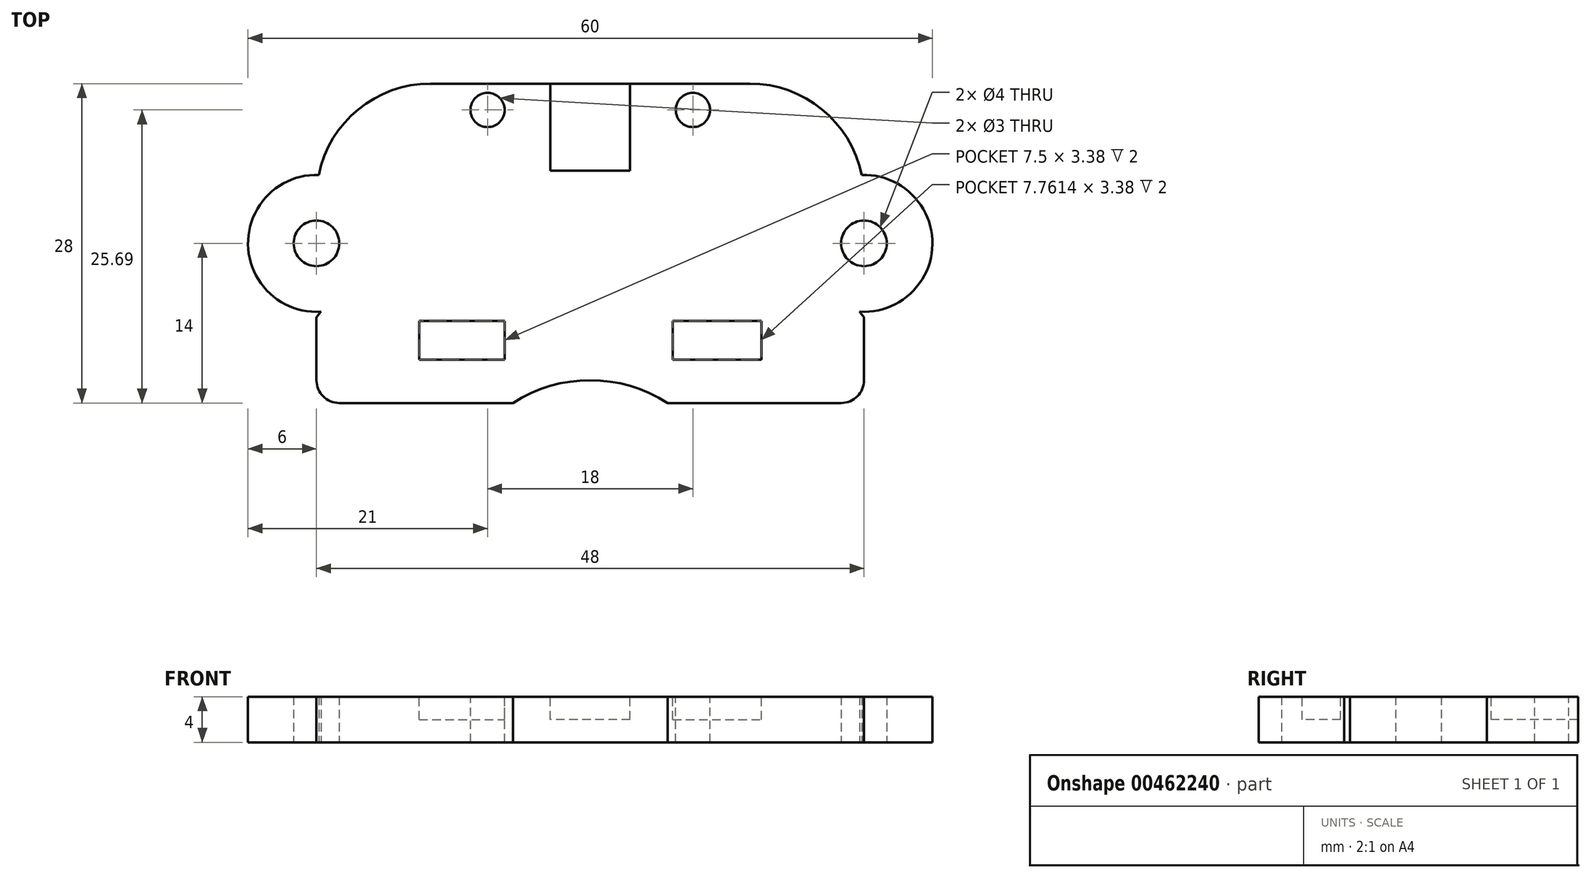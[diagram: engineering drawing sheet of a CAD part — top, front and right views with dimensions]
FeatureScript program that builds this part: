
annotation { "Feature Type Name" : "Feature", "Feature Type Description" : "" }
export const myFeature = defineFeature(function(context is Context, id is Id, definition is map)
    precondition{}
    {
        {
            var Q0;
            Q0=qCreatedBy(makeId("Top.planeOp"),FACE);
            var sketch = newSketch(context, id + "F0", { "sketchPlane" : qUnion([Q0])});
            skLineSegment(sketch, "E0.bottom", {"start": v(22, -14) * mm, "end": v(-22, -14) * mm});
            skLineSegment(sketch, "E0.top", {"start": v(14, 14) * mm, "end": v(-14, 14) * mm});
            skLineSegment(sketch, "E0.left", {"start": v(24, -12) * mm, "end": v(24, 4) * mm});
            skLineSegment(sketch, "E0.right", {"start": v(-24, -12) * mm, "end": v(-24, 4) * mm});
            skPoint(sketch, "E0.middle", {"position": v(0, 0) * mm});
            skPoint(sketch, "E1", {"position": v(-24, 0) * mm});
            skPoint(sketch, "E2", {"position": v(24, 0) * mm});
            skPoint(sketch, "E3", {"position": v(76.27, -6.83) * mm});
            skCircle(sketch, "E4", {"center": v(0, -24.5) * mm, "radius": 30 * mm});
            skCircle(sketch, "E5", {"center": v(0, -24.5) * mm, "radius": 12.5 * mm});
            skCircle(sketch, "E6", {"center": v(-24, 0) * mm, "radius": 4 * mm});
            skCircle(sketch, "E7", {"center": v(24, 0) * mm, "radius": 4 * mm});
            skCircle(sketch, "E8.0", {"center": v(-24, 0) * mm, "radius": 6 * mm});
            skCircle(sketch, "E9.0", {"center": v(24, 0) * mm, "radius": 6 * mm});
            skPoint(sketch, "E10.visualSharp", {"position": v(-24, 14) * mm});
            skArc(sketch, "E10.filletArc", {"start": v(-14, 14) * mm, "mid": v(-21.07, 11.07) * mm, "end": v(-24, 4) * mm});
            skPoint(sketch, "E11.visualSharp", {"position": v(24, 14) * mm});
            skArc(sketch, "E11.filletArc", {"start": v(24, 4) * mm, "mid": v(21.07, 11.07) * mm, "end": v(14, 14) * mm});
            skPoint(sketch, "E12.visualSharp", {"position": v(-24, -14) * mm});
            skArc(sketch, "E12.filletArc", {"start": v(-24, -12) * mm, "mid": v(-23.41, -13.41) * mm, "end": v(-22, -14) * mm});
            skPoint(sketch, "E13.visualSharp", {"position": v(24, -14) * mm});
            skArc(sketch, "E13.filletArc", {"start": v(22, -14) * mm, "mid": v(23.41, -13.41) * mm, "end": v(24, -12) * mm});
            skSolve(sketch);
        }
        {
            var Q0;
            {var subQ16=sQuery(id+"F0.wireOp",EDGE,"E12.filletArc");Q0=makeQuery(id+"F0.imprint","IMPRINT",FACE,{"disambiguationData":[TD([[makeQuery(id+"F0.imprint","IMPRINT",EDGE,{"derivedFrom":subQ16}),1.0]])]});}
            var Q1;
            {var subQ7=sQuery(id+"F0.wireOp",EDGE,"E0.top");Q1=makeQuery(id+"F0.imprint","IMPRINT",FACE,{"disambiguationData":[TD([[makeQuery(id+"F0.imprint","IMPRINT",EDGE,{"derivedFrom":subQ7}),1.0]])]});}
            var Q2;
            {var subQ0=sQuery(id+"F0.wireOp",EDGE,"E7");var subQ1=sQuery(id+"F0.wireOp",EDGE,"E0.left");var subQ3=makeQuery(id+"F0.imprint","INTERSECT",VERTEX,{"derivedFrom":[subQ1,subQ0]});Q2=makeQuery(id+"F0.imprint","IMPRINT",FACE,{"disambiguationData":[TD([[makeQuery(id+"F0.imprint","IMPRINT",EDGE,{"disambiguationData":[TD([[subQ3,-1.0]])],"derivedFrom":subQ1}),-1.0]])]});}
            var Q3;
            {var subQ0=sQuery(id+"F0.wireOp",EDGE,"E8.0");var subQ1=sQuery(id+"F0.wireOp",EDGE,"E4");var subQ2=makeQuery(id+"F0.imprint","INTERSECT",VERTEX,{"disambiguationData":[OD(0.0)],"derivedFrom":[subQ1,subQ0]});Q3=makeQuery(id+"F0.imprint","IMPRINT",FACE,{"disambiguationData":[TD([[makeQuery(id+"F0.imprint","IMPRINT",EDGE,{"disambiguationData":[TD([[subQ2,-1.0]])],"derivedFrom":subQ1}),1.0]])]});}
            var Q4;
            {var subQ2=sQuery(id+"F0.wireOp",EDGE,"E0.left");var subQ5=sQuery(id+"F0.wireOp",EDGE,"E9.0");var subQ9=makeQuery(id+"F0.imprint","INTERSECT",VERTEX,{"derivedFrom":[subQ2,subQ5]});Q4=makeQuery(id+"F0.imprint","IMPRINT",FACE,{"disambiguationData":[TD([[makeQuery(id+"F0.imprint","IMPRINT",EDGE,{"disambiguationData":[TD([[subQ9,-1.0]])],"derivedFrom":subQ2}),1.0]])]});}
            var Q5;
            {var subQ0=sQuery(id+"F0.wireOp",EDGE,"E8.0");var subQ1=sQuery(id+"F0.wireOp",EDGE,"E0.right");var subQ2=makeQuery(id+"F0.imprint","INTERSECT",VERTEX,{"derivedFrom":[subQ1,subQ0]});Q5=makeQuery(id+"F0.imprint","IMPRINT",FACE,{"disambiguationData":[TD([[makeQuery(id+"F0.imprint","IMPRINT",EDGE,{"disambiguationData":[TD([[subQ2,-1.0]])],"derivedFrom":subQ1}),1.0]])]});}
            var Q6;
            {var subQ0=sQuery(id+"F0.wireOp",EDGE,"E9.0");var subQ1=sQuery(id+"F0.wireOp",EDGE,"E0.left");var subQ2=makeQuery(id+"F0.imprint","INTERSECT",VERTEX,{"derivedFrom":[subQ1,subQ0]});Q6=makeQuery(id+"F0.imprint","IMPRINT",FACE,{"disambiguationData":[TD([[makeQuery(id+"F0.imprint","IMPRINT",EDGE,{"disambiguationData":[TD([[subQ2,-1.0]])],"derivedFrom":subQ1}),-1.0]])]});}
            var Q7;
            {var subQ2=sQuery(id+"F0.wireOp",EDGE,"E0.right");var subQ5=sQuery(id+"F0.wireOp",EDGE,"E8.0");var subQ6=makeQuery(id+"F0.imprint","INTERSECT",VERTEX,{"derivedFrom":[subQ2,subQ5]});Q7=makeQuery(id+"F0.imprint","IMPRINT",FACE,{"disambiguationData":[TD([[makeQuery(id+"F0.imprint","IMPRINT",EDGE,{"disambiguationData":[TD([[subQ6,-1.0]])],"derivedFrom":subQ2}),-1.0]])]});}
            var Q8;
            {var subQ0=sQuery(id+"F0.wireOp",EDGE,"E7");var subQ1=sQuery(id+"F0.wireOp",EDGE,"E0.left");var subQ3=makeQuery(id+"F0.imprint","INTERSECT",VERTEX,{"derivedFrom":[subQ1,subQ0]});Q8=makeQuery(id+"F0.imprint","IMPRINT",FACE,{"disambiguationData":[TD([[makeQuery(id+"F0.imprint","IMPRINT",EDGE,{"disambiguationData":[TD([[subQ3,-1.0]])],"derivedFrom":subQ1}),1.0]])]});}
            var Q9;
            {var subQ0=sQuery(id+"F0.wireOp",EDGE,"E6");var subQ1=sQuery(id+"F0.wireOp",EDGE,"E0.right");var subQ3=makeQuery(id+"F0.imprint","INTERSECT",VERTEX,{"derivedFrom":[subQ1,subQ0]});Q9=makeQuery(id+"F0.imprint","IMPRINT",FACE,{"disambiguationData":[TD([[makeQuery(id+"F0.imprint","IMPRINT",EDGE,{"disambiguationData":[TD([[subQ3,-1.0]])],"derivedFrom":subQ1}),-1.0]])]});}
            var Q10;
            {var subQ0=sQuery(id+"F0.wireOp",EDGE,"E6");var subQ1=sQuery(id+"F0.wireOp",EDGE,"E0.right");var subQ3=makeQuery(id+"F0.imprint","INTERSECT",VERTEX,{"derivedFrom":[subQ1,subQ0]});Q10=makeQuery(id+"F0.imprint","IMPRINT",FACE,{"disambiguationData":[TD([[makeQuery(id+"F0.imprint","IMPRINT",EDGE,{"disambiguationData":[TD([[subQ3,-1.0]])],"derivedFrom":subQ1}),1.0]])]});}
            var Q11;
            {var subQ0=sQuery(id+"F0.wireOp",EDGE,"E9.0");var subQ1=sQuery(id+"F0.wireOp",EDGE,"E4");var subQ2=makeQuery(id+"F0.imprint","INTERSECT",VERTEX,{"disambiguationData":[OD(0.0)],"derivedFrom":[subQ1,subQ0]});Q11=makeQuery(id+"F0.imprint","IMPRINT",FACE,{"disambiguationData":[TD([[makeQuery(id+"F0.imprint","IMPRINT",EDGE,{"disambiguationData":[TD([[subQ2,-1.0]])],"derivedFrom":subQ1}),1.0]])]});}
            extrude(context, id + "F1", {"entities" : qUnion([Q0, Q1, Q2, Q3, Q4, Q5, Q6, Q7, Q8, Q9, Q10, Q11]), "depth" : 4 * mm});
        }
        {
            var Q0;
            Q0=sQuery(id+"F0.wireOp",VERTEX,"E1");
            var Q1;
            Q1=sQuery(id+"F0.wireOp",VERTEX,"E2");
            var Q2;
            Q2=makeQuery(id+"F1.opExtrude","SWEPT_BODY",BODY,{"disambiguationData":[OSD([sQuery(id+"F0.wireOp",EDGE,"E0.bottom"),sQuery(id+"F0.wireOp",EDGE,"E0.top"),sQuery(id+"F0.wireOp",EDGE,"E0.left"),sQuery(id+"F0.wireOp",EDGE,"E0.right"),sQuery(id+"F0.wireOp",EDGE,"E4"),sQuery(id+"F0.wireOp",EDGE,"E5"),sQuery(id+"F0.wireOp",EDGE,"E8.0"),sQuery(id+"F0.wireOp",EDGE,"E9.0"),sQuery(id+"F0.wireOp",EDGE,"E10.filletArc"),sQuery(id+"F0.wireOp",EDGE,"E11.filletArc"),sQuery(id+"F0.wireOp",EDGE,"E12.filletArc"),sQuery(id+"F0.wireOp",EDGE,"E13.filletArc")])]});
            hole(context, id + "F2", {"style" : HoleStyle.SIMPLE, "endStyle" : HoleEndStyle.THROUGH, "oppositeDirection" : true, "holeDiameter" : 4 * mm, "isTappedThrough" : true, "tappedDepth" : 12 * mm, "tapClearance" : 3, "locations" : qUnion([Q0, Q1]), "scope" : qUnion([Q2])});
        }
        {
            var Q0;
            Q0=makeQuery(id+"F1.opExtrude","CAP_FACE",FACE,{"disambiguationData":[OSD([sQuery(id+"F0.wireOp",EDGE,"E0.bottom"),sQuery(id+"F0.wireOp",EDGE,"E0.top"),sQuery(id+"F0.wireOp",EDGE,"E0.left"),sQuery(id+"F0.wireOp",EDGE,"E0.right"),sQuery(id+"F0.wireOp",EDGE,"E4"),sQuery(id+"F0.wireOp",EDGE,"E5"),sQuery(id+"F0.wireOp",EDGE,"E8.0"),sQuery(id+"F0.wireOp",EDGE,"E9.0"),sQuery(id+"F0.wireOp",EDGE,"E10.filletArc"),sQuery(id+"F0.wireOp",EDGE,"E11.filletArc"),sQuery(id+"F0.wireOp",EDGE,"E12.filletArc"),sQuery(id+"F0.wireOp",EDGE,"E13.filletArc")])],"isStart":false});
            var sketch = newSketch(context, id + "F3", { "sketchPlane" : qUnion([Q0])});
            skLineSegment(sketch, "E14.bottom", {"start": v(-15, 10.19) * mm, "end": v(15, 10.19) * mm});
            skLineSegment(sketch, "E14.top", {"start": v(-15, -10.2) * mm, "end": v(15, -10.19) * mm});
            skLineSegment(sketch, "E14.left", {"start": v(-15, 10.19) * mm, "end": v(-15, -10.2) * mm});
            skLineSegment(sketch, "E14.right", {"start": v(15, 10.2) * mm, "end": v(15, -10.19) * mm});
            skPoint(sketch, "E14.middle", {"position": v(0, 0) * mm});
            skPoint(sketch, "E15", {"position": v(-7.5, -10.19) * mm});
            skPoint(sketch, "E16", {"position": v(7.5, -10.19) * mm});
            skPoint(sketch, "E17", {"position": v(-12, -6.81) * mm});
            skPoint(sketch, "E18", {"position": v(12, -6.8) * mm});
            skLineSegment(sketch, "E19.bottom", {"start": v(-15, -10.2) * mm, "end": v(-7.5, -10.2) * mm});
            skLineSegment(sketch, "E19.top", {"start": v(-15, -6.81) * mm, "end": v(-7.5, -6.81) * mm});
            skLineSegment(sketch, "E19.left", {"start": v(-15, -10.2) * mm, "end": v(-15, -6.81) * mm});
            skLineSegment(sketch, "E19.right", {"start": v(-7.5, -10.19) * mm, "end": v(-7.5, -6.81) * mm});
            skLineSegment(sketch, "E20.bottom", {"start": v(15, -10.19) * mm, "end": v(7.24, -10.19) * mm});
            skLineSegment(sketch, "E20.top", {"start": v(15, -6.8) * mm, "end": v(7.24, -6.81) * mm});
            skLineSegment(sketch, "E20.left", {"start": v(15, -10.19) * mm, "end": v(15, -6.8) * mm});
            skLineSegment(sketch, "E20.right", {"start": v(7.24, -10.2) * mm, "end": v(7.24, -6.8) * mm});
            skLineSegment(sketch, "E21.bottom", {"start": v(3.5, 14) * mm, "end": v(-3.5, 14) * mm});
            skLineSegment(sketch, "E21.top", {"start": v(3.5, 6.38) * mm, "end": v(-3.5, 6.38) * mm});
            skLineSegment(sketch, "E21.left", {"start": v(3.5, 14) * mm, "end": v(3.5, 6.38) * mm});
            skLineSegment(sketch, "E21.right", {"start": v(-3.5, 14) * mm, "end": v(-3.5, 6.38) * mm});
            skPoint(sketch, "E21.middle", {"position": v(0, 10.2) * mm});
            skPoint(sketch, "E22", {"position": v(-9, 11.69) * mm});
            skPoint(sketch, "E23", {"position": v(9, 11.7) * mm});
            skCircle(sketch, "E24", {"center": v(-9, 11.69) * mm, "radius": 1.5 * mm});
            skCircle(sketch, "E25", {"center": v(9, 11.7) * mm, "radius": 1.5 * mm});
            skSolve(sketch);
        }
        {
            var Q0;
            Q0=makeQuery(id+"F3.imprint","IMPRINT",FACE,{"disambiguationData":[TD([[makeQuery(id+"F3.imprint","IMPRINT",EDGE,{"derivedFrom":sQuery(id+"F3.wireOp",EDGE,"E14.top")}),1.0]])]});
            var Q1;
            {var subQ5=sQuery(id+"F3.wireOp",EDGE,"E21.bottom");Q1=makeQuery(id+"F3.imprint","IMPRINT",FACE,{"disambiguationData":[TD([[makeQuery(id+"F3.imprint","IMPRINT",EDGE,{"derivedFrom":subQ5}),1.0]])]});}
            var Q2;
            {var subQ5=sQuery(id+"F3.wireOp",EDGE,"E21.top");Q2=makeQuery(id+"F3.imprint","IMPRINT",FACE,{"disambiguationData":[TD([[makeQuery(id+"F3.imprint","IMPRINT",EDGE,{"derivedFrom":subQ5}),-1.0]])]});}
            extrude(context, id + "F4", {"entities" : qUnion([Q0, Q1, Q2]), "operationType" : NewBodyOperationType.REMOVE, "oppositeDirection" : true, "depth" : 2 * mm});
        }
        {
            var Q0;
            Q0=sQuery(id+"F3.wireOp",VERTEX,"E22");
            var Q1;
            Q1=sQuery(id+"F3.wireOp",VERTEX,"E23");
            var Q2;
            Q2=makeQuery(id+"F1.opExtrude","SWEPT_BODY",BODY,{"disambiguationData":[OSD([sQuery(id+"F0.wireOp",EDGE,"E0.bottom"),sQuery(id+"F0.wireOp",EDGE,"E0.top"),sQuery(id+"F0.wireOp",EDGE,"E0.left"),sQuery(id+"F0.wireOp",EDGE,"E0.right"),sQuery(id+"F0.wireOp",EDGE,"E4"),sQuery(id+"F0.wireOp",EDGE,"E5"),sQuery(id+"F0.wireOp",EDGE,"E8.0"),sQuery(id+"F0.wireOp",EDGE,"E9.0"),sQuery(id+"F0.wireOp",EDGE,"E10.filletArc"),sQuery(id+"F0.wireOp",EDGE,"E11.filletArc"),sQuery(id+"F0.wireOp",EDGE,"E12.filletArc"),sQuery(id+"F0.wireOp",EDGE,"E13.filletArc")])]});
            hole(context, id + "F5", {"style" : HoleStyle.SIMPLE, "endStyle" : HoleEndStyle.BLIND, "holeDiameter" : 3 * mm, "holeDepth" : 4 * mm, "isTappedThrough" : true, "tappedDepth" : 12 * mm, "tapClearance" : 3, "locations" : qUnion([Q0, Q1]), "scope" : qUnion([Q2])});
        }
        {
            var Q0;
            Q0=makeQuery(id+"F3.imprint","IMPRINT",FACE,{"disambiguationData":[TD([[makeQuery(id+"F3.imprint","IMPRINT",EDGE,{"derivedFrom":sQuery(id+"F3.wireOp",EDGE,"E14.top")}),-1.0]])]});
            var sketch = newSketch(context, id + "F6", { "sketchPlane" : qUnion([Q0])});
            skSolve(sketch);
        }
        {
            var Q0;
            Q0=makeQuery(id+"F6.imprint","IMPRINT",FACE,{"disambiguationData":[TD([[makeQuery(id+"F6.imprint","IMPRINT",EDGE,{"derivedFrom":makeQuery(id+"F3.imprint","IMPRINT",EDGE,{"derivedFrom":sQuery(id+"F3.wireOp",EDGE,"E25")})}),1.0]])]});
            var Q1;
            Q1=makeQuery(id+"F6.imprint","IMPRINT",FACE,{"disambiguationData":[TD([[makeQuery(id+"F6.imprint","IMPRINT",EDGE,{"derivedFrom":makeQuery(id+"F3.imprint","IMPRINT",EDGE,{"derivedFrom":sQuery(id+"F3.wireOp",EDGE,"E24")})}),1.0]])]});
            extrude(context, id + "F7", {"entities" : qUnion([Q0, Q1]), "oppositeDirection" : true, "depth" : 4 * mm, "offsetDistance" : 25 * mm});
        }
    });
